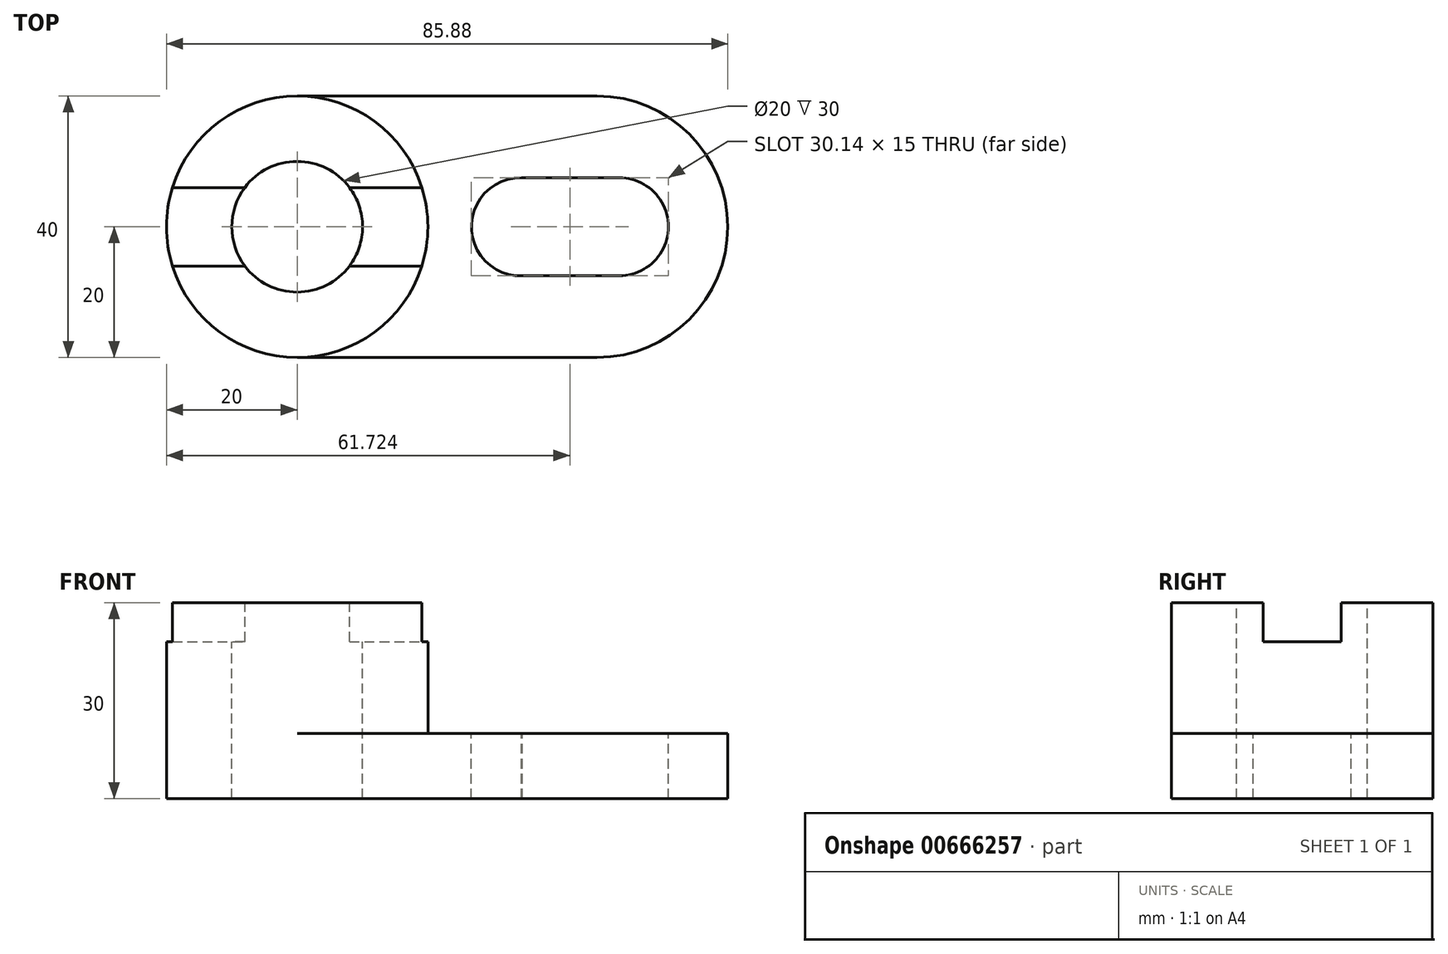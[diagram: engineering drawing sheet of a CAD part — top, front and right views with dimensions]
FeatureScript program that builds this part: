
annotation { "Feature Type Name" : "Feature", "Feature Type Description" : "" }
export const myFeature = defineFeature(function(context is Context, id is Id, definition is map)
    precondition{}
    {
        {
            var Q0;
            Q0=qCreatedBy(makeId("Top.planeOp"),FACE);
            var sketch = newSketch(context, id + "F0", { "sketchPlane" : qUnion([Q0])});
            skArc(sketch, "E0", {"start": v(0, 20) * mm, "mid": v(-20, 0) * mm, "end": v(0, -20) * mm});
            skArc(sketch, "E1", {"start": v(45.88, -20) * mm, "mid": v(65.88, 0) * mm, "end": v(45.88, 20) * mm});
            skLineSegment(sketch, "E2", {"start": v(0, 20) * mm, "end": v(45.88, 20) * mm});
            skLineSegment(sketch, "E3", {"start": v(0, -20) * mm, "end": v(45.88, -20) * mm});
            skSolve(sketch);
        }
        {
            var Q0;
            Q0=qSketchRegion(id+"F0",true);
            extrude(context, id + "F1", {"entities" : qUnion([Q0]), "depth" : 10 * mm, "offsetDistance" : 25 * mm});
        }
        {
            var Q0;
            Q0=makeQuery(id+"F1.opExtrude","CAP_FACE",FACE,{"disambiguationData":[OSD([sQuery(id+"F0.wireOp",EDGE,"E0"),sQuery(id+"F0.wireOp",EDGE,"E1"),sQuery(id+"F0.wireOp",EDGE,"E2"),sQuery(id+"F0.wireOp",EDGE,"E3")])],"isStart":false});
            var sketch = newSketch(context, id + "F2", { "sketchPlane" : qUnion([Q0])});
            skCircle(sketch, "E4", {"center": v(0, 0) * mm, "radius": 20 * mm});
            skSolve(sketch);
        }
        {
            var Q0;
            {var subQ0=sQuery(id+"F2.wireOp",EDGE,"E4");var subQ1=makeQuery(id+"F2.imprint","INTERSECT",VERTEX,{"derivedFrom":[makeQuery(id+"F1.opExtrude","CAP_EDGE",EDGE,{"disambiguationData":[OSD([sQuery(id+"F0.wireOp",EDGE,"E2")])],"isStart":false}),subQ0]});Q0=makeQuery(id+"F2.imprint","IMPRINT",FACE,{"disambiguationData":[TD([[makeQuery(id+"F2.imprint","IMPRINT",EDGE,{"disambiguationData":[TD([[subQ1,-1.0]])],"derivedFrom":subQ0}),1.0]])]});}
            extrude(context, id + "F3", {"entities" : qUnion([Q0]), "operationType" : NewBodyOperationType.ADD, "depth" : 20 * mm, "offsetDistance" : 25 * mm});
        }
        {
            var Q0;
            Q0=makeQuery(id+"F3.opExtrude","CAP_FACE",FACE,{"disambiguationData":[OSD([sQuery(id+"F2.wireOp",EDGE,"E4")])],"isStart":false});
            var sketch = newSketch(context, id + "F4", { "sketchPlane" : qUnion([Q0])});
            skCircle(sketch, "E5", {"center": v(0, 0) * mm, "radius": 10 * mm});
            skSolve(sketch);
        }
        {
            var Q0;
            Q0=qSketchRegion(id+"F4",true);
            extrude(context, id + "F5", {"entities" : qUnion([Q0]), "operationType" : NewBodyOperationType.REMOVE, "oppositeDirection" : true, "depth" : 93.7 * mm, "offsetDistance" : 25 * mm});
        }
        {
            var Q0;
            Q0=makeQuery(id+"F3.opExtrude","CAP_FACE",FACE,{"disambiguationData":[OSD([sQuery(id+"F2.wireOp",EDGE,"E4")])],"isStart":false});
            var sketch = newSketch(context, id + "F6", { "sketchPlane" : qUnion([Q0])});
            skLineSegment(sketch, "E6.bottom", {"start": v(-25, 6) * mm, "end": v(25, 6) * mm});
            skLineSegment(sketch, "E6.top", {"start": v(-25, -6) * mm, "end": v(25, -6) * mm});
            skLineSegment(sketch, "E6.left", {"start": v(-25, 6) * mm, "end": v(-25, -6) * mm});
            skLineSegment(sketch, "E6.right", {"start": v(25, 6) * mm, "end": v(25, -6) * mm});
            skSolve(sketch);
        }
        {
            var Q0;
            Q0=qSketchRegion(id+"F6",true);
            extrude(context, id + "F7", {"entities" : qUnion([Q0]), "operationType" : NewBodyOperationType.REMOVE, "oppositeDirection" : true, "depth" : 6 * mm, "offsetDistance" : 25 * mm});
        }
        {
            var Q0;
            Q0=makeQuery(id+"F1.opExtrude","CAP_FACE",FACE,{"disambiguationData":[OSD([sQuery(id+"F0.wireOp",EDGE,"E0"),sQuery(id+"F0.wireOp",EDGE,"E1"),sQuery(id+"F0.wireOp",EDGE,"E2"),sQuery(id+"F0.wireOp",EDGE,"E3")])],"isStart":false});
            var sketch = newSketch(context, id + "F8", { "sketchPlane" : qUnion([Q0])});
            skArc(sketch, "E7", {"start": v(34.3, 7.5) * mm, "mid": v(26.65, -0.06) * mm, "end": v(34.42, -7.5) * mm});
            skArc(sketch, "E8", {"start": v(49.3, -7.5) * mm, "mid": v(56.8, 0) * mm, "end": v(49.3, 7.5) * mm});
            skLineSegment(sketch, "E9", {"start": v(34.3, 7.5) * mm, "end": v(49.3, 7.5) * mm});
            skLineSegment(sketch, "E10", {"start": v(33.88, -7.5) * mm, "end": v(49.3, -7.5) * mm});
            skSolve(sketch);
        }
        {
            var Q0;
            {var subQ5=sQuery(id+"F8.wireOp",EDGE,"E8");Q0=makeQuery(id+"F8.imprint","IMPRINT",FACE,{"disambiguationData":[TD([[makeQuery(id+"F8.imprint","IMPRINT",EDGE,{"derivedFrom":subQ5}),1.0]])]});}
            var sketch = newSketch(context, id + "F9", { "sketchPlane" : qUnion([Q0])});
            skSolve(sketch);
        }
        {
            var Q0;
            Q0=qSketchRegion(id+"F8",true);
            var Q1;
            {var subQ5=sQuery(id+"F8.wireOp",EDGE,"E8");Q1=makeQuery(id+"F9.imprint","IMPRINT",FACE,{"disambiguationData":[TD([[makeQuery(id+"F9.imprint","IMPRINT",EDGE,{"derivedFrom":makeQuery(id+"F8.imprint","IMPRINT",EDGE,{"derivedFrom":subQ5})}),1.0]])]});}
            extrude(context, id + "F10", {"entities" : qUnion([Q0, Q1]), "operationType" : NewBodyOperationType.REMOVE, "oppositeDirection" : true, "depth" : 28.9 * mm, "offsetDistance" : 25 * mm});
        }
    });
